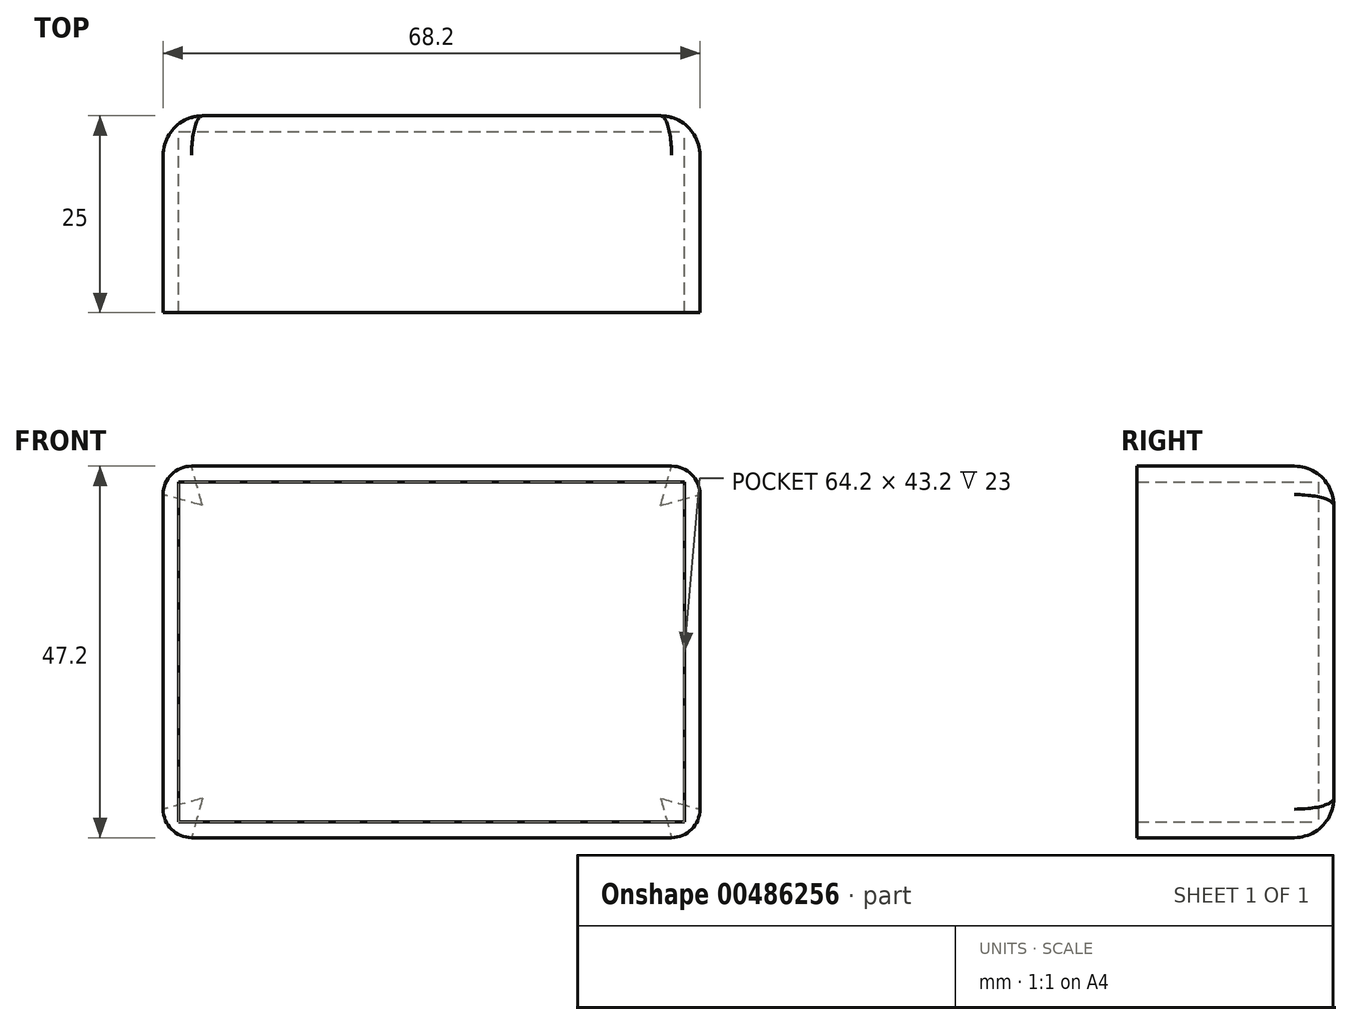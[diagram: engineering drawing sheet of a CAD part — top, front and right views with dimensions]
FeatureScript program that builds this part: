
annotation { "Feature Type Name" : "Feature", "Feature Type Description" : "" }
export const myFeature = defineFeature(function(context is Context, id is Id, definition is map)
    precondition{}
    {
        {
            var Q0;
            Q0=qCreatedBy(makeId("Front.planeOp"),FACE);
            var sketch = newSketch(context, id + "F0", { "sketchPlane" : qUnion([Q0])});
            skLineSegment(sketch, "E0.bottom", {"start": v(-59.06, 13.3) * mm, "end": v(5.14, 13.3) * mm});
            skLineSegment(sketch, "E0.top", {"start": v(-59.06, -29.9) * mm, "end": v(5.14, -29.9) * mm});
            skLineSegment(sketch, "E0.left", {"start": v(-59.06, 13.3) * mm, "end": v(-59.06, -29.9) * mm});
            skLineSegment(sketch, "E0.right", {"start": v(5.14, 13.3) * mm, "end": v(5.14, -29.9) * mm});
            skLineSegment(sketch, "E1.bottom", {"start": v(-61.06, 15.3) * mm, "end": v(7.14, 15.3) * mm});
            skLineSegment(sketch, "E1.top", {"start": v(-61.06, -31.9) * mm, "end": v(7.14, -31.9) * mm});
            skLineSegment(sketch, "E1.left", {"start": v(-61.06, 15.3) * mm, "end": v(-61.06, -31.9) * mm});
            skLineSegment(sketch, "E1.right", {"start": v(7.14, 15.3) * mm, "end": v(7.14, -31.9) * mm});
            skSolve(sketch);
        }
        {
            var Q0;
            Q0=makeQuery(id+"F0.imprint","IMPRINT",FACE,{"disambiguationData":[TD([[makeQuery(id+"F0.imprint","IMPRINT",EDGE,{"derivedFrom":sQuery(id+"F0.wireOp",EDGE,"E0.bottom")}),-1.0]])]});
            extrude(context, id + "F1", {"entities" : qUnion([Q0]), "depth" : 2 * mm});
        }
        {
            var Q0;
            Q0 = qSketchRegion(id + "F0", true);
            extrude(context, id + "F2", {"entities" : qUnion([Q0]), "operationType" : NewBodyOperationType.ADD, "depth" : 25 * mm});
        }
        {
            var Q0;
            {var subQ0=sQuery(id+"F0.wireOp",EDGE,"E0.right");var subQ1=sQuery(id+"F0.wireOp",EDGE,"E0.left");var subQ2=sQuery(id+"F0.wireOp",EDGE,"E0.top");var subQ3=sQuery(id+"F0.wireOp",EDGE,"E0.bottom");Q0=makeQuery(id+"F2.boolean.opBoolean","MERGE",FACE,{"derivedFrom":[makeQuery(id+"F1.opExtrude","CAP_FACE",FACE,{"disambiguationData":[OSD([subQ3,subQ2,subQ1,subQ0])],"isStart":true}),makeQuery(id+"F2.opExtrude","CAP_FACE",FACE,{"disambiguationData":[OSD([subQ3,subQ2,subQ1,subQ0,sQuery(id+"F0.wireOp",EDGE,"E1.bottom"),sQuery(id+"F0.wireOp",EDGE,"E1.top"),sQuery(id+"F0.wireOp",EDGE,"E1.left"),sQuery(id+"F0.wireOp",EDGE,"E1.right")])],"isStart":true})]});}
            fillet(context, id + "F3", {"entities" : qUnion([Q0]), "radius" : 5 * mm, "tangentPropagation" : true, "allowEdgeOverflow" : false});
        }
        {
            var Q0;
            Q0=makeQuery(id+"F2.opExtrude","SWEPT_EDGE",EDGE,{"disambiguationData":[OSD([sQuery(id+"F0.wireOp",EDGE,"E1.top"),sQuery(id+"F0.wireOp",EDGE,"E1.left")])]});
            var Q1;
            Q1=makeQuery(id+"F2.opExtrude","SWEPT_EDGE",EDGE,{"disambiguationData":[OSD([sQuery(id+"F0.wireOp",EDGE,"E1.bottom"),sQuery(id+"F0.wireOp",EDGE,"E1.left")])]});
            var Q2;
            Q2=makeQuery(id+"F2.opExtrude","SWEPT_EDGE",EDGE,{"disambiguationData":[OSD([sQuery(id+"F0.wireOp",EDGE,"E1.bottom"),sQuery(id+"F0.wireOp",EDGE,"E1.right")])]});
            var Q3;
            Q3=makeQuery(id+"F2.opExtrude","SWEPT_EDGE",EDGE,{"disambiguationData":[OSD([sQuery(id+"F0.wireOp",EDGE,"E1.top"),sQuery(id+"F0.wireOp",EDGE,"E1.right")])]});
            fillet(context, id + "F4", {"entities" : qUnion([Q0, Q1, Q2, Q3]), "radius" : 3.62 * mm, "tangentPropagation" : true, "allowEdgeOverflow" : false});
        }
    });
